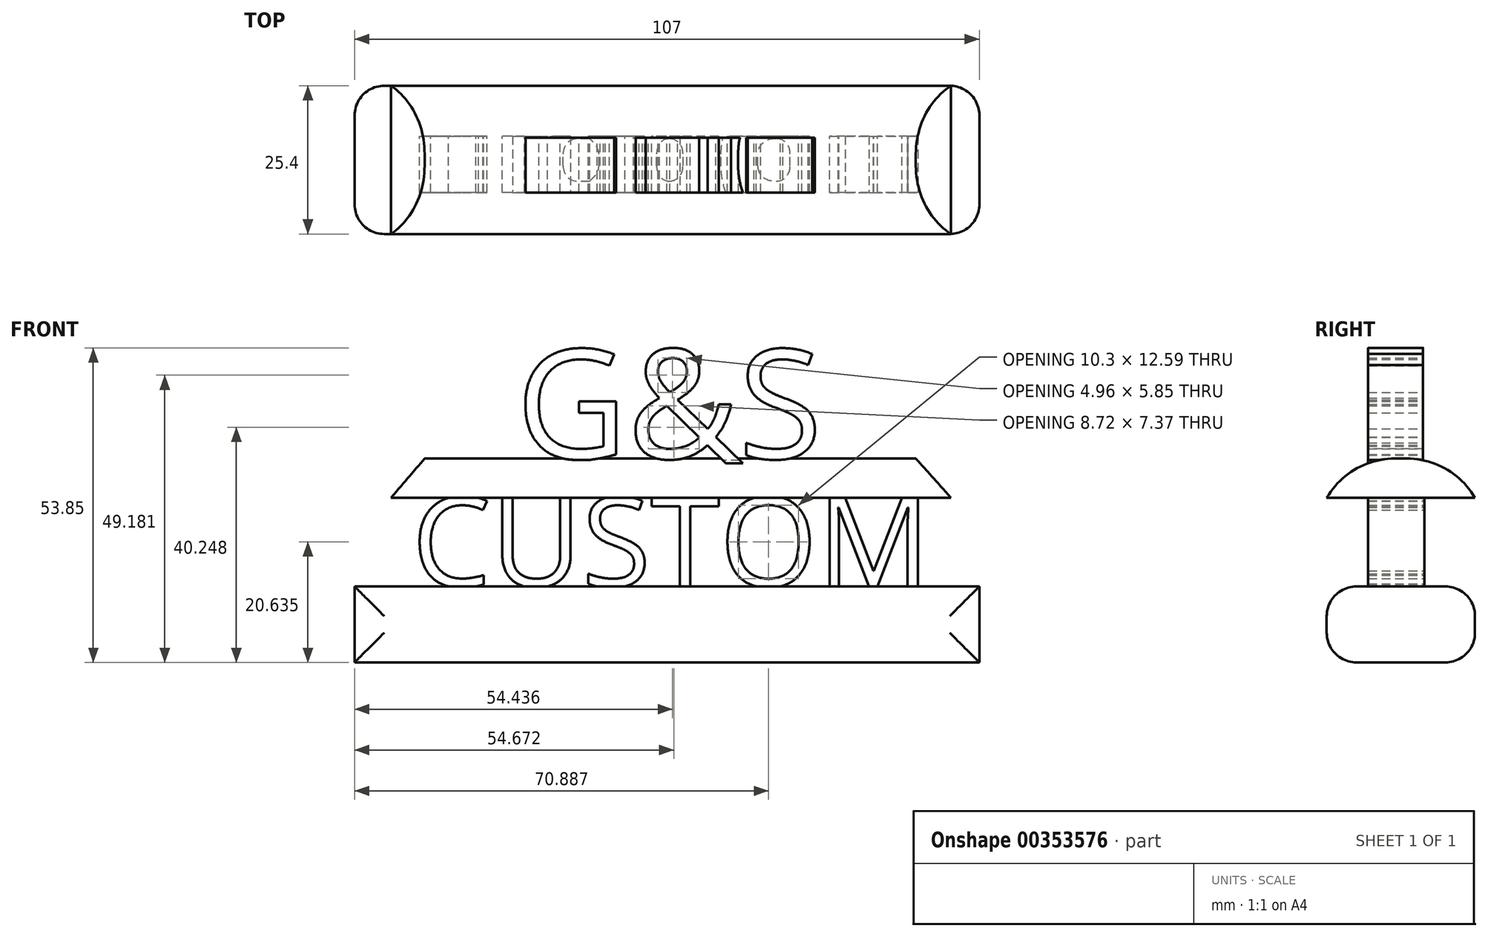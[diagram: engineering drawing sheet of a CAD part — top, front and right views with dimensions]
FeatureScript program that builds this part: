
annotation { "Feature Type Name" : "Feature", "Feature Type Description" : "" }
export const myFeature = defineFeature(function(context is Context, id is Id, definition is map)
    precondition{}
    {
        {
            var Q0;
            Q0=qCreatedBy(makeId("Front.planeOp"),FACE);
            var sketch = newSketch(context, id + "F0", { "sketchPlane" : qUnion([Q0])});
            skLineSegment(sketch, "E0.bottom", {"start": v(-50.37, -32.3) * mm, "end": v(56.63, -32.3) * mm});
            skLineSegment(sketch, "E0.top", {"start": v(-50.37, -19.28) * mm, "end": v(56.63, -19.28) * mm});
            skLineSegment(sketch, "E0.left", {"start": v(-50.37, -32.3) * mm, "end": v(-50.37, -19.28) * mm});
            skLineSegment(sketch, "E0.right", {"start": v(56.63, -32.3) * mm, "end": v(56.63, -19.28) * mm});
            skSolve(sketch);
        }
        {
            var Q0;
            Q0 = qSketchRegion(id + "F0", true);
            extrude(context, id + "F1", {"entities" : qUnion([Q0]), "depth" : 25.4 * mm});
        }
        {
            var Q0;
            Q0=qCreatedBy(makeId("Front.planeOp"),FACE);
            var sketch = newSketch(context, id + "F2", { "sketchPlane" : qUnion([Q0])});
            skText(sketch, "E1", { "text": "CUSTOM", "fontName": "OpenSans-Regular.ttf"});
            const initialGuessF2  = {"E1": [-0.04053, -0.0193, 1, 0, 0.01542]};
            skSetInitialGuess(sketch, initialGuessF2);
            skSolve(sketch);
        }
        {
            var Q0;
            Q0 = qSketchRegion(id + "F2", true);
            extrude(context, id + "F3", {"entities" : qUnion([Q0]), "operationType" : NewBodyOperationType.ADD, "depth" : 18.29 * mm, "hasSecondDirection" : true, "secondDirectionOppositeDirection" : false, "secondDirectionDepth" : 8.64 * mm});
        }
        {
            var Q0;
            Q0=qCreatedBy(makeId("Front.planeOp"),FACE);
            var sketch = newSketch(context, id + "F4", { "sketchPlane" : qUnion([Q0])});
            skLineSegment(sketch, "E2", {"start": v(-44.15, -4.12) * mm, "end": v(51.77, -4.12) * mm});
            skLineSegment(sketch, "E3", {"start": v(-44.15, -4.12) * mm, "end": v(-38.36, 2.63) * mm});
            skLineSegment(sketch, "E4", {"start": v(45.74, 2.63) * mm, "end": v(51.77, -4.12) * mm});
            skLineSegment(sketch, "E5", {"start": v(-38.36, 2.63) * mm, "end": v(45.74, 2.63) * mm});
            skSolve(sketch);
        }
        {
            var Q0;
            Q0 = qSketchRegion(id + "F4", true);
            extrude(context, id + "F5", {"entities" : qUnion([Q0]), "operationType" : NewBodyOperationType.ADD, "depth" : 25.4 * mm});
        }
        {
            var Q0;
            Q0=qCreatedBy(makeId("Front.planeOp"),FACE);
            var sketch = newSketch(context, id + "F6", { "sketchPlane" : qUnion([Q0])});
            skText(sketch, "E6", { "text": "G&S\n", "fontName": "OpenSans-Regular.ttf"});
            const initialGuessF6  = {"E6": [-0.0227, 0.00263, 1, 0, 0.0188]};
            skSetInitialGuess(sketch, initialGuessF6);
            skSolve(sketch);
        }
        {
            var Q0;
            Q0 = qSketchRegion(id + "F6", true);
            extrude(context, id + "F7", {"entities" : qUnion([Q0]), "operationType" : NewBodyOperationType.ADD, "depth" : 18.29 * mm, "hasSecondDirection" : true, "secondDirectionOppositeDirection" : false, "secondDirectionDepth" : 8.9 * mm});
        }
        {
            var Q0;
            Q0=makeQuery(id+"F1.opExtrude","CAP_FACE",FACE,{"disambiguationData":[OSD([sQuery(id+"F0.wireOp",EDGE,"E0.bottom"),sQuery(id+"F0.wireOp",EDGE,"E0.top"),sQuery(id+"F0.wireOp",EDGE,"E0.left"),sQuery(id+"F0.wireOp",EDGE,"E0.right")])],"isStart":false});
            var Q1;
            Q1=makeQuery(id+"F1.opExtrude","CAP_FACE",FACE,{"disambiguationData":[OSD([sQuery(id+"F0.wireOp",EDGE,"E0.bottom"),sQuery(id+"F0.wireOp",EDGE,"E0.top"),sQuery(id+"F0.wireOp",EDGE,"E0.left"),sQuery(id+"F0.wireOp",EDGE,"E0.right")])],"isStart":true});
            fillet(context, id + "F8", {"entities" : qUnion([Q0, Q1]), "radius" : 5.08 * mm, "tangentPropagation" : true, "allowEdgeOverflow" : false});
        }
        {
            var Q0;
            Q0=makeQuery(id+"F5.opExtrude","CAP_EDGE",EDGE,{"disambiguationData":[OSD([sQuery(id+"F4.wireOp",EDGE,"E5")])],"isStart":false});
            var Q1;
            Q1=makeQuery(id+"F5.opExtrude","CAP_EDGE",EDGE,{"disambiguationData":[OSD([sQuery(id+"F4.wireOp",EDGE,"E5")])],"isStart":true});
            fillet(context, id + "F9", {"entities" : qUnion([Q0, Q1]), "radius" : 13.5 * mm, "tangentPropagation" : true, "allowEdgeOverflow" : false});
        }
    });
